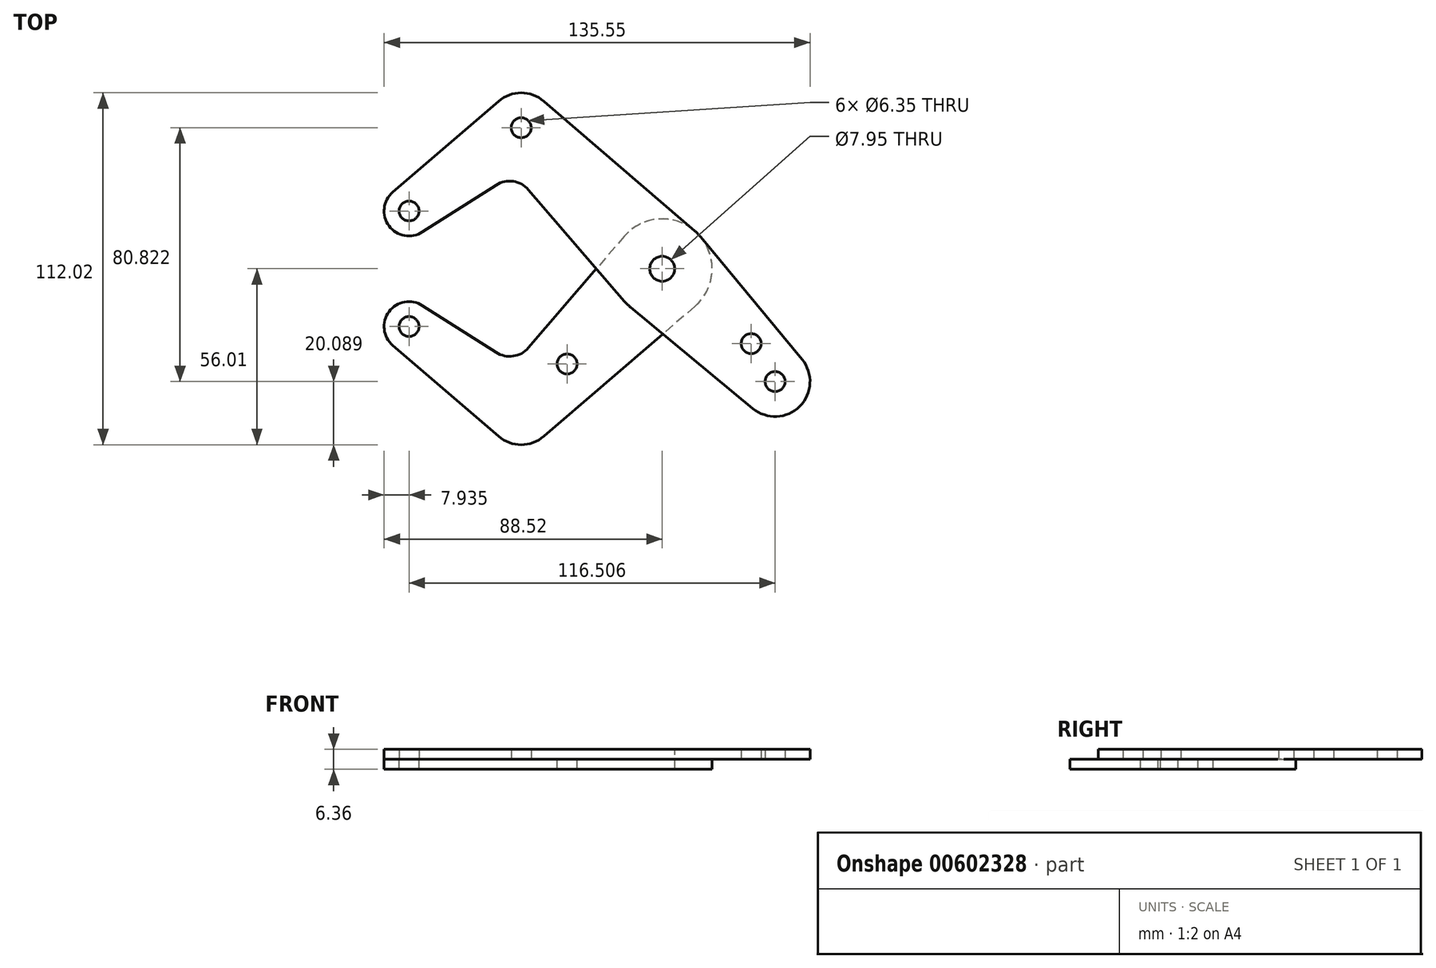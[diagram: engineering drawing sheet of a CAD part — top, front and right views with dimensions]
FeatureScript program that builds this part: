
annotation { "Feature Type Name" : "Feature", "Feature Type Description" : "" }
export const myFeature = defineFeature(function(context is Context, id is Id, definition is map)
    precondition{}
    {
        {
            var Q0;
            Q0=qCreatedBy(makeId("Top.planeOp"),FACE);
            var sketch = newSketch(context, id + "F0", { "sketchPlane" : qUnion([Q0])});
            skCircle(sketch, "E0", {"center": v(0, 0) * mm, "radius": 15.88 * mm});
            skCircle(sketch, "E1", {"center": v(-44.9, 44.9) * mm, "radius": 11.11 * mm});
            skCircle(sketch, "E2", {"center": v(35.92, -35.92) * mm, "radius": 11.11 * mm});
            skCircle(sketch, "E3", {"center": v(-80.59, 18.4) * mm, "radius": 7.94 * mm});
            skLineSegment(sketch, "E4", {"start": v(-85.76, 24.42) * mm, "end": v(-52.15, 53.33) * mm});
            skLineSegment(sketch, "E5", {"start": v(-76.32, 11.7) * mm, "end": v(-52.86, 26.65) * mm});
            skLineSegment(sketch, "E6", {"start": v(-42.56, 25.13) * mm, "end": v(-12.04, -10.35) * mm});
            skLineSegment(sketch, "E7", {"start": v(-37.66, 53.33) * mm, "end": v(10.35, 12.04) * mm});
            skLineSegment(sketch, "E8", {"start": v(12.23, 10.12) * mm, "end": v(44.6, -28.98) * mm});
            skLineSegment(sketch, "E9", {"start": v(-10.12, -12.23) * mm, "end": v(28.83, -44.48) * mm});
            skPoint(sketch, "E10.orphan", {"position": v(10.85, 11.8) * mm});
            skLineSegment(sketch, "E11", {"start": v(-52.78, 52.78) * mm, "end": v(-52.76, 52.76) * mm, "construction": true});
            skLineSegment(sketch, "E12", {"start": v(-35.76, 51.7) * mm, "end": v(-35.98, 51.53) * mm, "construction": true});
            skCircle(sketch, "E13", {"center": v(28.32, -23.83) * mm, "radius": 3.18 * mm});
            skArc(sketch, "E14.filletArc", {"start": v(-42.56, 25.13) * mm, "mid": v(-47.42, 27.82) * mm, "end": v(-52.86, 26.65) * mm});
            skCircle(sketch, "E15", {"center": v(-44.9, 44.9) * mm, "radius": 3.18 * mm});
            skCircle(sketch, "E16", {"center": v(-80.59, 18.4) * mm, "radius": 3.18 * mm});
            skCircle(sketch, "E17", {"center": v(35.92, -35.92) * mm, "radius": 3.18 * mm});
            skCircle(sketch, "E18", {"center": v(0, 0) * mm, "radius": 3.98 * mm});
            skCircle(sketch, "E19", {"center": v(0, 0) * mm, "radius": 3.18 * mm});
            skLineSegment(sketch, "E20", {"start": v(-80.59, 18.4) * mm, "end": v(-80.59, -18.4) * mm, "construction": true});
            skCircle(sketch, "E21", {"center": v(-80.59, -18.4) * mm, "radius": 7.94 * mm});
            skCircle(sketch, "E22", {"center": v(-80.59, -18.4) * mm, "radius": 3.18 * mm});
            skCircle(sketch, "E23", {"center": v(-44.9, -44.9) * mm, "radius": 11.11 * mm});
            skLineSegment(sketch, "E24", {"start": v(0, 0) * mm, "end": v(-44.9, -44.9) * mm, "construction": true});
            skLineSegment(sketch, "E25.trimOffspring", {"start": v(-47.15, 47.15) * mm, "end": v(38.17, -38.17) * mm, "construction": true});
            skLineSegment(sketch, "E26.trimOffspring", {"start": v(-42.35, 46.8) * mm, "end": v(-83.13, 16.5) * mm, "construction": true});
            skLineSegment(sketch, "E27", {"start": v(-44.9, 44.9) * mm, "end": v(-44.9, -44.9) * mm, "construction": true});
            skLineSegment(sketch, "E28", {"start": v(-80.59, -18.4) * mm, "end": v(-44.9, -44.9) * mm, "construction": true});
            skLineSegment(sketch, "E29", {"start": v(12.3, -10.35) * mm, "end": v(-37.66, -53.33) * mm});
            skLineSegment(sketch, "E30", {"start": v(-11.26, 11.26) * mm, "end": v(-42.56, -25.13) * mm});
            skLineSegment(sketch, "E31", {"start": v(-52.86, -26.65) * mm, "end": v(-80.59, -8.99) * mm});
            skLineSegment(sketch, "E32", {"start": v(-52.15, -53.33) * mm, "end": v(-85.76, -24.42) * mm});
            skPoint(sketch, "E33.orphan", {"position": v(10.85, 11.6) * mm});
            skCircle(sketch, "E34", {"center": v(-30.3, -30.3) * mm, "radius": 3.18 * mm});
            skArc(sketch, "E35.filletArc", {"start": v(-52.86, -26.65) * mm, "mid": v(-47.42, -27.82) * mm, "end": v(-42.56, -25.13) * mm});
            skSolve(sketch);
        }
        {
            var Q0;
            {var subQ14=sQuery(id+"F0.wireOp",EDGE,"E32");Q0=makeQuery(id+"F0.imprint","IMPRINT",FACE,{"disambiguationData":[TD([[makeQuery(id+"F0.imprint","IMPRINT",EDGE,{"derivedFrom":subQ14}),-1.0]])]});}
            var Q1;
            {var subQ0=sQuery(id+"F0.wireOp",EDGE,"E23");var subQ1=makeQuery(id+"F0.imprint","INTERSECT",VERTEX,{"derivedFrom":[subQ0,sQuery(id+"F0.wireOp",EDGE,"E29")]});Q1=makeQuery(id+"F0.imprint","IMPRINT",FACE,{"disambiguationData":[TD([[makeQuery(id+"F0.imprint","IMPRINT",EDGE,{"disambiguationData":[TD([[subQ1,1.0]])],"derivedFrom":subQ0}),1.0]])]});}
            var Q2;
            Q2=makeQuery(id+"F0.imprint","IMPRINT",FACE,{"disambiguationData":[TD([[makeQuery(id+"F0.imprint","IMPRINT",EDGE,{"derivedFrom":sQuery(id+"F0.wireOp",EDGE,"E22")}),-1.0]])]});
            var Q3;
            {var subQ0=sQuery(id+"F0.wireOp",EDGE,"E9");var subQ1=sQuery(id+"F0.wireOp",EDGE,"E0");var subQ2=makeQuery(id+"F0.imprint","INTERSECT",VERTEX,{"derivedFrom":[subQ1,subQ0]});Q3=makeQuery(id+"F0.imprint","IMPRINT",FACE,{"disambiguationData":[TD([[makeQuery(id+"F0.imprint","IMPRINT",EDGE,{"disambiguationData":[TD([[subQ2,-1.0]])],"derivedFrom":subQ1}),-1.0]])]});}
            var Q4;
            {var subQ0=sQuery(id+"F0.wireOp",EDGE,"E6");var subQ1=sQuery(id+"F0.wireOp",EDGE,"E0");var subQ2=makeQuery(id+"F0.imprint","INTERSECT",VERTEX,{"derivedFrom":[subQ1,subQ0]});Q4=makeQuery(id+"F0.imprint","IMPRINT",FACE,{"disambiguationData":[TD([[makeQuery(id+"F0.imprint","IMPRINT",EDGE,{"disambiguationData":[TD([[subQ2,1.0]])],"derivedFrom":subQ1}),-1.0]])]});}
            var Q5;
            Q5=makeQuery(id+"F0.imprint","IMPRINT",FACE,{"disambiguationData":[TD([[makeQuery(id+"F0.imprint","IMPRINT",EDGE,{"derivedFrom":sQuery(id+"F0.wireOp",EDGE,"E18")}),-1.0]])]});
            extrude(context, id + "F1", {"entities" : qUnion([Q0, Q1, Q2, Q3, Q4, Q5]), "oppositeDirection" : true, "depth" : 3.17 * mm, "offsetDistance" : 25.4 * mm});
        }
        {
            var Q0;
            {var subQ0=sQuery(id+"F0.wireOp",EDGE,"E4");Q0=makeQuery(id+"F0.imprint","IMPRINT",FACE,{"disambiguationData":[TD([[makeQuery(id+"F0.imprint","IMPRINT",EDGE,{"derivedFrom":subQ0}),-1.0]])]});}
            var Q1;
            Q1=makeQuery(id+"F0.imprint","IMPRINT",FACE,{"disambiguationData":[TD([[makeQuery(id+"F0.imprint","IMPRINT",EDGE,{"derivedFrom":sQuery(id+"F0.wireOp",EDGE,"E16")}),-1.0]])]});
            var Q2;
            Q2=makeQuery(id+"F0.imprint","IMPRINT",FACE,{"disambiguationData":[TD([[makeQuery(id+"F0.imprint","IMPRINT",EDGE,{"derivedFrom":sQuery(id+"F0.wireOp",EDGE,"E15")}),-1.0]])]});
            var Q3;
            Q3=makeQuery(id+"F0.imprint","IMPRINT",FACE,{"disambiguationData":[TD([[makeQuery(id+"F0.imprint","IMPRINT",EDGE,{"derivedFrom":sQuery(id+"F0.wireOp",EDGE,"E18")}),-1.0]])]});
            var Q4;
            {var subQ0=sQuery(id+"F0.wireOp",EDGE,"E6");var subQ1=sQuery(id+"F0.wireOp",EDGE,"E0");var subQ2=makeQuery(id+"F0.imprint","INTERSECT",VERTEX,{"derivedFrom":[subQ1,subQ0]});Q4=makeQuery(id+"F0.imprint","IMPRINT",FACE,{"disambiguationData":[TD([[makeQuery(id+"F0.imprint","IMPRINT",EDGE,{"disambiguationData":[TD([[subQ2,1.0]])],"derivedFrom":subQ1}),-1.0]])]});}
            var Q5;
            {var subQ0=sQuery(id+"F0.wireOp",EDGE,"E9");var subQ1=sQuery(id+"F0.wireOp",EDGE,"E0");var subQ2=makeQuery(id+"F0.imprint","INTERSECT",VERTEX,{"derivedFrom":[subQ1,subQ0]});Q5=makeQuery(id+"F0.imprint","IMPRINT",FACE,{"disambiguationData":[TD([[makeQuery(id+"F0.imprint","IMPRINT",EDGE,{"disambiguationData":[TD([[subQ2,-1.0]])],"derivedFrom":subQ1}),-1.0]])]});}
            var Q6;
            {var subQ3=sQuery(id+"F0.wireOp",EDGE,"E13");Q6=makeQuery(id+"F0.imprint","IMPRINT",FACE,{"disambiguationData":[TD([[makeQuery(id+"F0.imprint","IMPRINT",EDGE,{"derivedFrom":subQ3}),-1.0]])]});}
            var Q7;
            Q7=makeQuery(id+"F0.imprint","IMPRINT",FACE,{"disambiguationData":[TD([[makeQuery(id+"F0.imprint","IMPRINT",EDGE,{"derivedFrom":sQuery(id+"F0.wireOp",EDGE,"E17")}),-1.0]])]});
            extrude(context, id + "F2", {"entities" : qUnion([Q0, Q1, Q2, Q3, Q4, Q5, Q6, Q7]), "operationType" : NewBodyOperationType.ADD, "depth" : 3.17 * mm, "offsetDistance" : 25.4 * mm});
        }
    });
